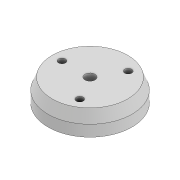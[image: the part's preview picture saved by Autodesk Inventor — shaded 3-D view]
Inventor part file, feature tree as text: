
AUTODESK INVENTOR PART (.ipt)
format: ipt  version: 2020.3 (Build 243373000, 373)  size: 104,448 bytes
history: native  units: mm
features: extrude x1, chamfer x1, sketch x1
ambient origin geometry x8: Origin, YZ Plane, XZ Plane, XY Plane, X Axis, Y Axis, Z Axis, Center Point
bodies: Solid1 (feature_tree)
feature tree (3):
  extrude  "Extrusion1"  Depth=10.0mm
  chamfer  "Chamfer1"  Distance=2.5mm
  sketch  "Sketch1"  dims[d1=3.6mm d2=30.0mm d3=8.660254mm d4=10.0mm d5=10.0mm d6=10.0mm d7=2.5mm d8=2.5mm d9=2.5mm d10=8.0mm d11=0.0mm d12=1.5mm d13=4.0mm d14=45.0deg]
